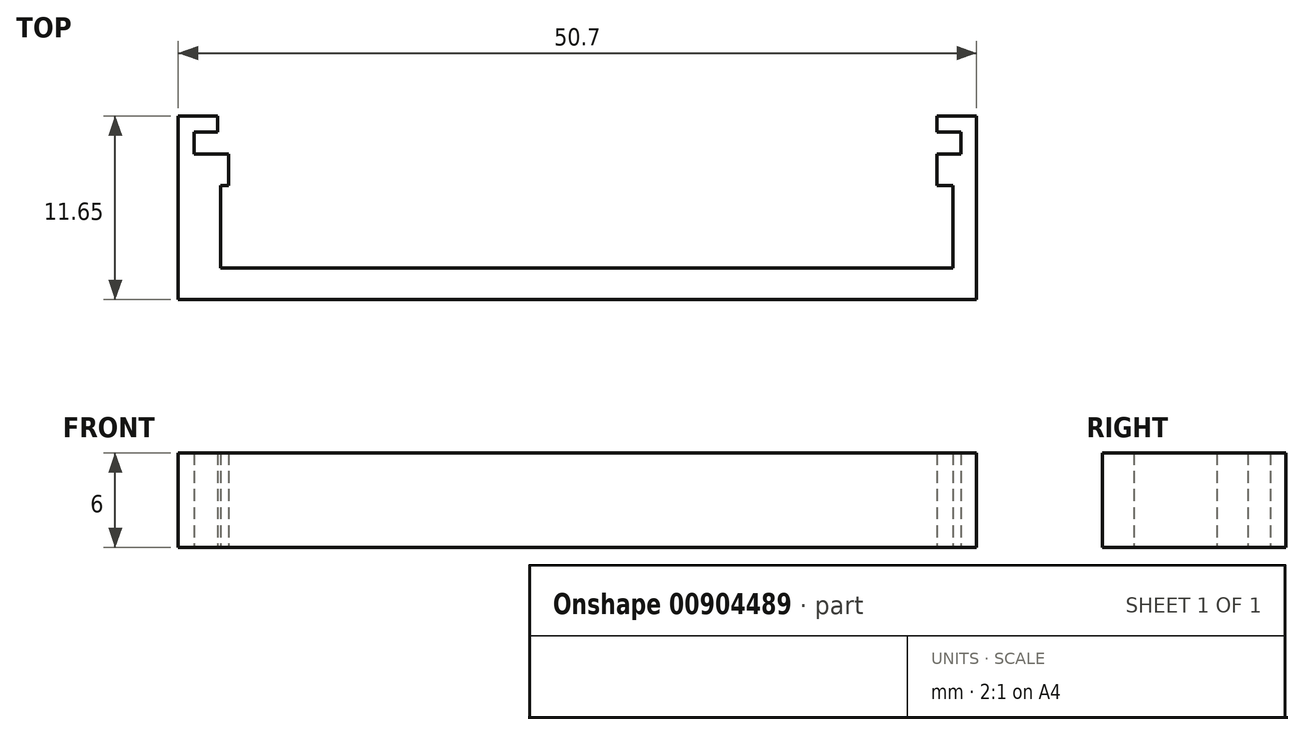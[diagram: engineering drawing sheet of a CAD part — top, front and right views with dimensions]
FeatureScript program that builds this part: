
annotation { "Feature Type Name" : "Feature", "Feature Type Description" : "" }
export const myFeature = defineFeature(function(context is Context, id is Id, definition is map)
    precondition{}
    {
        {
            var Q0;
            Q0=qCreatedBy(makeId("Top.planeOp"),FACE);
            var sketch = newSketch(context, id + "F0", { "sketchPlane" : qUnion([Q0])});
            skLineSegment(sketch, "E0", {"start": v(-25.35, 0) * mm, "end": v(25.35, 0) * mm});
            skLineSegment(sketch, "E1", {"start": v(25.35, 0) * mm, "end": v(25.35, 11.65) * mm});
            skLineSegment(sketch, "E2", {"start": v(25.35, 11.65) * mm, "end": v(22.85, 11.65) * mm});
            skLineSegment(sketch, "E3", {"start": v(22.85, 11.65) * mm, "end": v(22.85, 10.65) * mm});
            skLineSegment(sketch, "E4", {"start": v(22.85, 10.65) * mm, "end": v(24.35, 10.65) * mm});
            skLineSegment(sketch, "E5", {"start": v(24.35, 10.65) * mm, "end": v(24.35, 9.25) * mm});
            skLineSegment(sketch, "E6", {"start": v(24.35, 9.25) * mm, "end": v(22.85, 9.25) * mm});
            skLineSegment(sketch, "E7", {"start": v(22.85, 9.25) * mm, "end": v(22.85, 7.25) * mm});
            skLineSegment(sketch, "E8", {"start": v(22.85, 7.25) * mm, "end": v(23.85, 7.25) * mm});
            skLineSegment(sketch, "E9", {"start": v(23.85, 7.25) * mm, "end": v(23.85, 2) * mm});
            skLineSegment(sketch, "E10", {"start": v(23.85, 2) * mm, "end": v(-22.65, 2) * mm});
            skLineSegment(sketch, "E11", {"start": v(-22.65, 2) * mm, "end": v(-22.65, 7.25) * mm});
            skLineSegment(sketch, "E12", {"start": v(-22.15, 9.25) * mm, "end": v(-24.35, 9.25) * mm});
            skLineSegment(sketch, "E13", {"start": v(-24.35, 9.25) * mm, "end": v(-24.35, 10.65) * mm});
            skLineSegment(sketch, "E14", {"start": v(-24.35, 10.65) * mm, "end": v(-22.85, 10.65) * mm});
            skLineSegment(sketch, "E15", {"start": v(-22.85, 10.65) * mm, "end": v(-22.85, 11.65) * mm});
            skLineSegment(sketch, "E16", {"start": v(-22.85, 11.65) * mm, "end": v(-25.35, 11.65) * mm});
            skLineSegment(sketch, "E17", {"start": v(-25.35, 11.65) * mm, "end": v(-25.35, 0) * mm});
            skLineSegment(sketch, "E18", {"start": v(-24.35, 10.65) * mm, "end": v(-25.35, 10.65) * mm, "construction": true});
            skLineSegment(sketch, "E19", {"start": v(24.35, 10.65) * mm, "end": v(25.35, 10.65) * mm, "construction": true});
            skLineSegment(sketch, "E20", {"start": v(23.85, 2) * mm, "end": v(23.85, 0) * mm, "construction": true});
            skLineSegment(sketch, "E21", {"start": v(-22.65, 7.25) * mm, "end": v(-22.15, 7.25) * mm});
            skLineSegment(sketch, "E22", {"start": v(-22.15, 7.25) * mm, "end": v(-22.15, 9.25) * mm});
            skSolve(sketch);
        }
        {
            var Q0;
            Q0=makeQuery(id+"F0.imprint","IMPRINT",FACE,{"disambiguationData":[TD([[makeQuery(id+"F0.imprint","IMPRINT",EDGE,{"derivedFrom":sQuery(id+"F0.wireOp",EDGE,"E0")}),1.0]])]});
            extrude(context, id + "F1", {"entities" : qUnion([Q0]), "depth" : 6 * mm, "offsetDistance" : 25 * mm});
        }
    });
